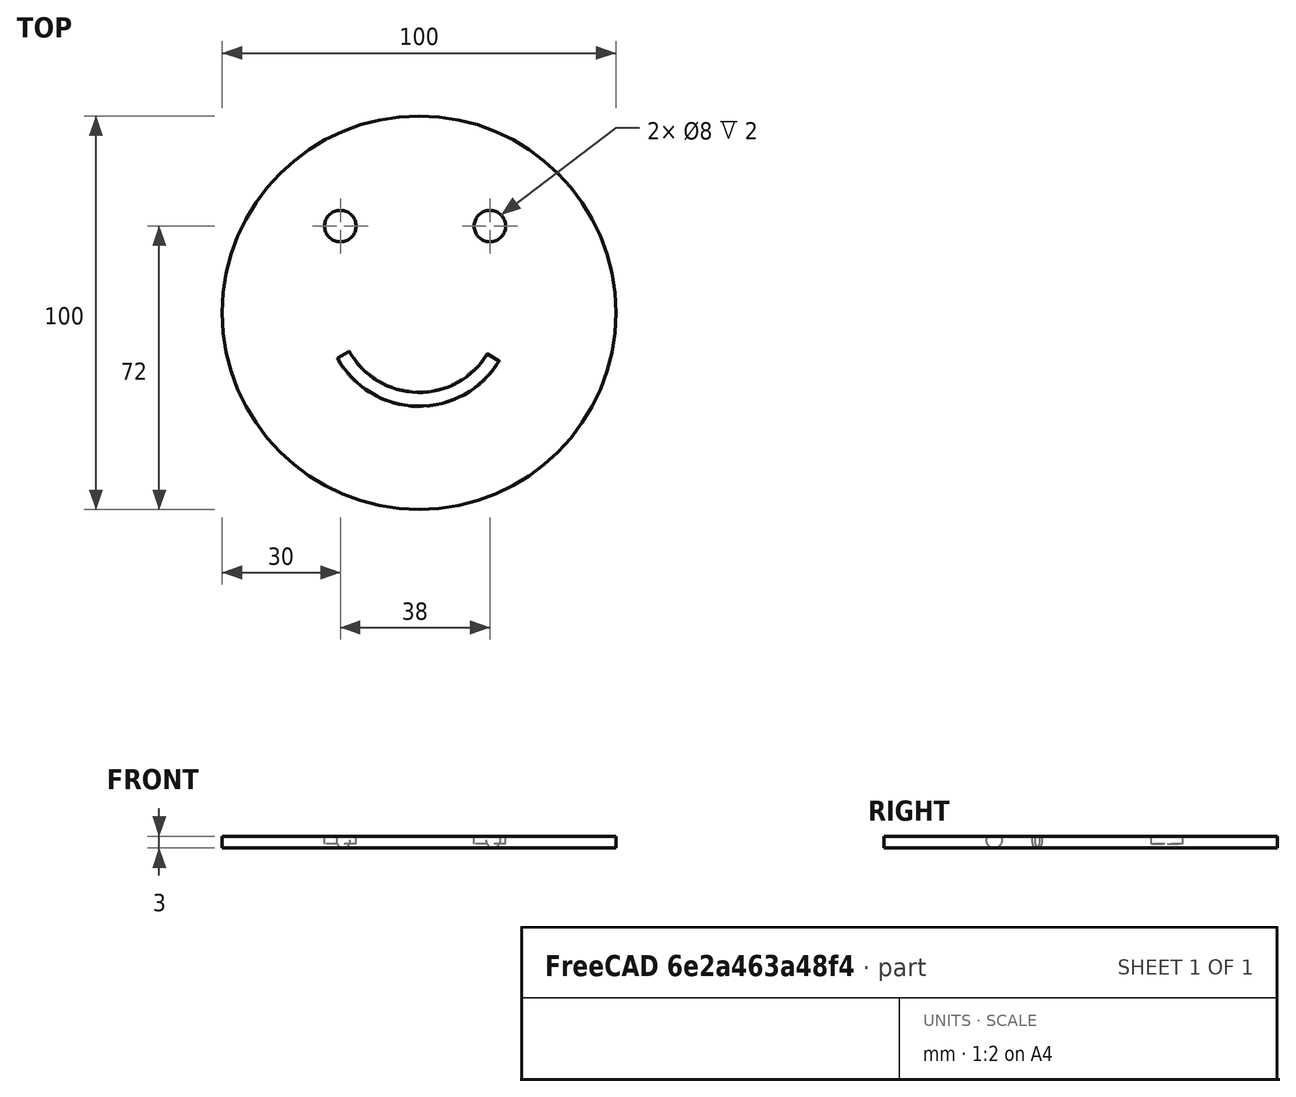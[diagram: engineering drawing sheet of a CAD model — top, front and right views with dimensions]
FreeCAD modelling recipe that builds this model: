
FCSTD DOCUMENT  (FreeCAD 0.16R6707 (Git))
Label: Smiley
License: CreativeCommons Attribution-ShareAlike
LicenseURL: http://creativecommons.org/licenses/by-sa/4.0/
objects: Part::Cylinder×3, Part::MultiFuse×2, Part::Torus×1, Part::Cut×1
note: 7 computed .brp shape members not serialized (recipe doc carries the construction recipe); baked Part::Feature solids carry a one-line shape summary decoded from their .brp

FEATURE [Part::Cylinder] Cylinder  label="Cara"
  Angle = 360
  Height = 3
  Radius = 50
FEATURE [Part::Cylinder] Cylinder001  label="Cylinder"
  Angle = 360
  Height = 10
  Placement = pos=(-20,22,1) rot=(0,0,1;0rad)
  Radius = 4
FEATURE [Part::Cylinder] Cylinder002  label="Cylinder001"
  Angle = 360
  Height = 10
  Placement = pos=(18,22,1) rot=(0,0,1;0rad)
  Radius = 4
FEATURE [Part::MultiFuse] Fusion  label="Ojos"
  Shapes = -> [Cylinder001,Cylinder002]
FEATURE [Part::Torus] Torus
  Angle1 = -180
  Angle2 = 180
  Angle3 = 120
  Placement = pos=(0,0,2) rot=(0,0,1;3.64774rad)
  Radius1 = 22
  Radius2 = 2
FEATURE [Part::MultiFuse] Fusion001  label="Ojos_Boca"
  Shapes = -> [Fusion,Torus]
FEATURE [Part::Cut] Cut  label="Smiley"
  Base = -> Cylinder
  Tool = -> Fusion001
